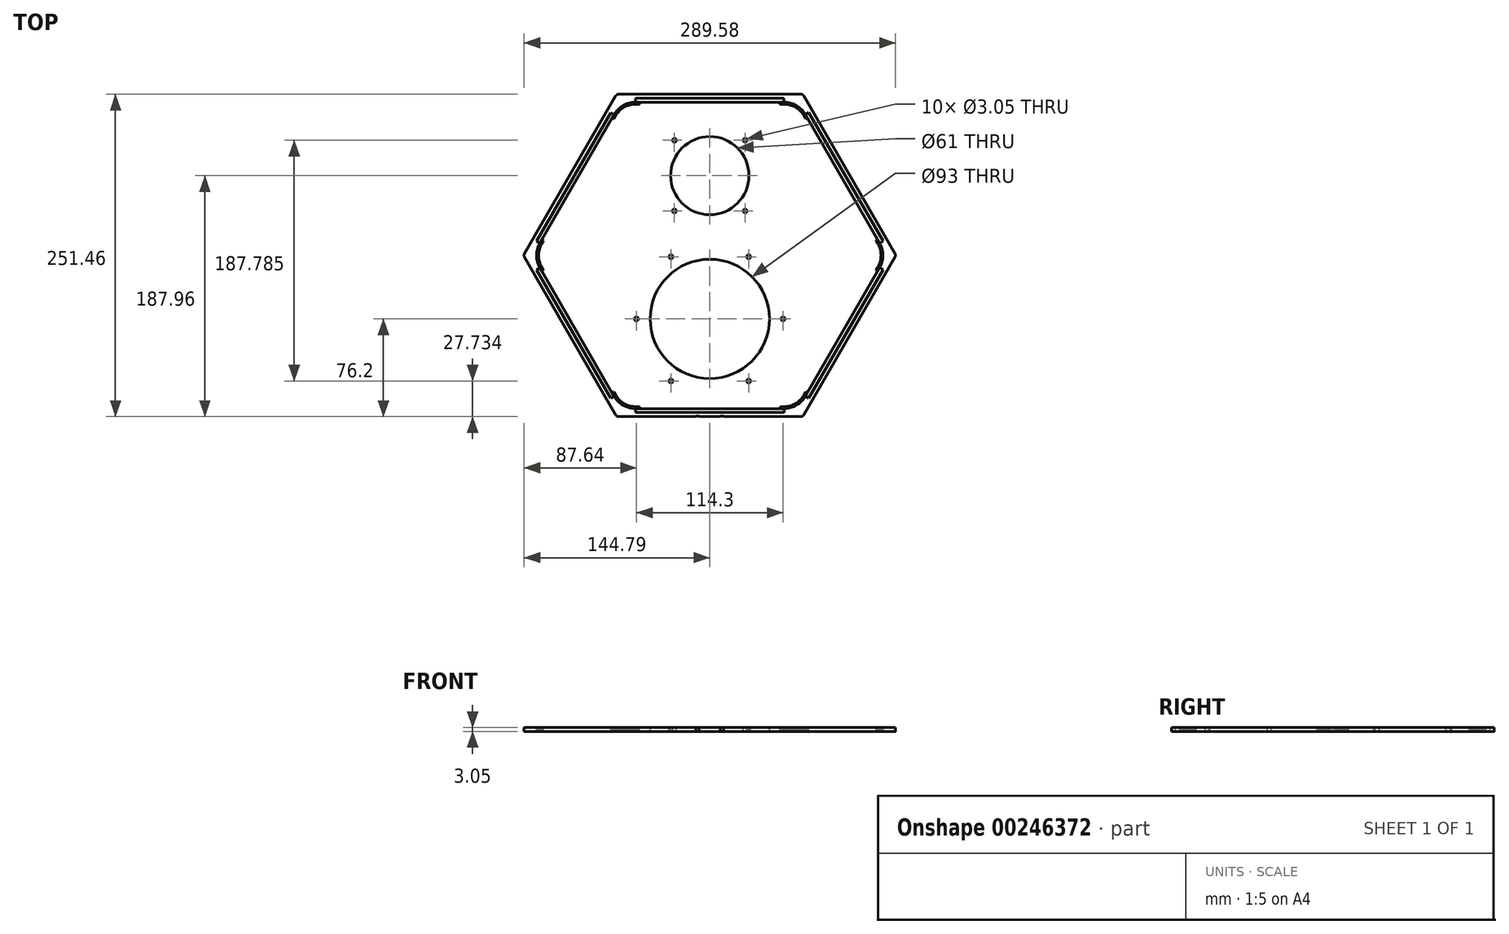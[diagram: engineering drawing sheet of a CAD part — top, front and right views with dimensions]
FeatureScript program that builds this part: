
annotation { "Feature Type Name" : "Feature", "Feature Type Description" : "" }
export const myFeature = defineFeature(function(context is Context, id is Id, definition is map)
    precondition{}
    {
        {
            var Q0;
            Q0=qCreatedBy(makeId("Top.planeOp"),FACE);
            var sketch = newSketch(context, id + "F0", { "sketchPlane" : qUnion([Q0])});
            skCircle(sketch, "E0.cCircle", {"center": v(0, 0) * mm, "radius": 125.73 * mm, "construction": true});
            skLineSegment(sketch, "E0.0", {"start": v(-137.85, 12.7) * mm, "end": v(-79.92, 113.03) * mm});
            skLineSegment(sketch, "E0.1", {"start": v(-57.93, 125.73) * mm, "end": v(57.93, 125.73) * mm});
            skLineSegment(sketch, "E0.2", {"start": v(79.92, 113.03) * mm, "end": v(137.85, 12.7) * mm});
            skLineSegment(sketch, "E0.3", {"start": v(137.85, -12.7) * mm, "end": v(79.92, -113.03) * mm});
            skLineSegment(sketch, "E0.4", {"start": v(57.93, -125.73) * mm, "end": v(-57.93, -125.73) * mm});
            skLineSegment(sketch, "E0.5", {"start": v(-79.92, -113.03) * mm, "end": v(-137.85, -12.7) * mm});
            skPoint(sketch, "E0.0.midPoint", {"position": v(-108.89, 62.87) * mm});
            skPoint(sketch, "E1.visualSharp", {"position": v(-72.6, 125.73) * mm});
            skArc(sketch, "E1.filletArc", {"start": v(-57.93, 125.73) * mm, "mid": v(-70.63, 122.33) * mm, "end": v(-79.92, 113.03) * mm});
            skPoint(sketch, "E2.visualSharp", {"position": v(72.6, 125.73) * mm});
            skArc(sketch, "E2.filletArc", {"start": v(79.92, 113.03) * mm, "mid": v(70.63, 122.33) * mm, "end": v(57.93, 125.73) * mm});
            skPoint(sketch, "E3.visualSharp", {"position": v(145.18, 0) * mm});
            skArc(sketch, "E3.filletArc", {"start": v(137.85, -12.7) * mm, "mid": v(141.25, 0) * mm, "end": v(137.85, 12.7) * mm});
            skPoint(sketch, "E4.visualSharp", {"position": v(72.6, -125.73) * mm});
            skArc(sketch, "E4.filletArc", {"start": v(57.93, -125.73) * mm, "mid": v(70.63, -122.33) * mm, "end": v(79.92, -113.03) * mm});
            skPoint(sketch, "E5.visualSharp", {"position": v(-72.6, -125.73) * mm});
            skArc(sketch, "E5.filletArc", {"start": v(-79.92, -113.03) * mm, "mid": v(-70.63, -122.33) * mm, "end": v(-57.93, -125.73) * mm});
            skPoint(sketch, "E6.visualSharp", {"position": v(-145.18, 0) * mm});
            skArc(sketch, "E6.filletArc", {"start": v(-137.85, 12.7) * mm, "mid": v(-141.25, 0) * mm, "end": v(-137.85, -12.7) * mm});
            skSolve(sketch);
        }
        {
            var Q0;
            Q0=qSketchRegion(id+"F0",true);
            extrude(context, id + "F1", {"entities" : qUnion([Q0]), "depth" : 3.05 * mm});
        }
        {
            var Q0;
            Q0=makeQuery(id+"F1.opExtrude","CAP_FACE",FACE,{"disambiguationData":[OSD([sQuery(id+"F0.wireOp",EDGE,"E0.0"),sQuery(id+"F0.wireOp",EDGE,"E0.1"),sQuery(id+"F0.wireOp",EDGE,"E0.2"),sQuery(id+"F0.wireOp",EDGE,"E0.3"),sQuery(id+"F0.wireOp",EDGE,"E0.4"),sQuery(id+"F0.wireOp",EDGE,"E0.5"),sQuery(id+"F0.wireOp",EDGE,"E1.filletArc"),sQuery(id+"F0.wireOp",EDGE,"E2.filletArc"),sQuery(id+"F0.wireOp",EDGE,"E3.filletArc"),sQuery(id+"F0.wireOp",EDGE,"E4.filletArc"),sQuery(id+"F0.wireOp",EDGE,"E5.filletArc"),sQuery(id+"F0.wireOp",EDGE,"E6.filletArc")])],"isStart":false});
            var sketch = newSketch(context, id + "F2", { "sketchPlane" : qUnion([Q0])});
            skCircle(sketch, "E7", {"center": v(0, 62.23) * mm, "radius": 30.5 * mm});
            skCircle(sketch, "E8", {"center": v(0, -49.53) * mm, "radius": 46.5 * mm});
            skLineSegment(sketch, "E9", {"start": v(-77.97, -49.53) * mm, "end": v(84.44, -49.53) * mm, "construction": true});
            skCircle(sketch, "E10", {"center": v(0, -49.53) * mm, "radius": 61.65 * mm, "construction": true});
            skCircle(sketch, "E11", {"center": v(0, -49.53) * mm, "radius": 57.15 * mm, "construction": true});
            skCircle(sketch, "E12", {"center": v(57.15, -49.53) * mm, "radius": 1.52 * mm});
            skLineSegment(sketch, "E13", {"start": v(0, -49.53) * mm, "end": v(0, -25.93) * mm, "construction": true});
            skLineSegment(sketch, "E14", {"start": v(0, -49.53) * mm, "end": v(30.28, -1.06) * mm, "construction": true});
            skLineSegment(sketch, "E15", {"start": v(0, -49.53) * mm, "end": v(30.28, -98) * mm, "construction": true});
            skCircle(sketch, "E16", {"center": v(30.28, -1.06) * mm, "radius": 1.52 * mm});
            skCircle(sketch, "E17", {"center": v(30.28, -98) * mm, "radius": 1.52 * mm});
            skCircle(sketch, "E18.MirrorC", {"center": v(-30.28, -1.06) * mm, "radius": 1.52 * mm});
            skCircle(sketch, "E19.MirrorC", {"center": v(-30.28, -98) * mm, "radius": 1.52 * mm});
            skCircle(sketch, "E20.MirrorC", {"center": v(-57.15, -49.53) * mm, "radius": 1.52 * mm});
            skCircle(sketch, "E21", {"center": v(0, 62.23) * mm, "radius": 38.97 * mm, "construction": true});
            skLineSegment(sketch, "E22", {"start": v(0, 62.23) * mm, "end": v(-27.56, 89.79) * mm, "construction": true});
            skCircle(sketch, "E23", {"center": v(-27.56, 89.79) * mm, "radius": 1.52 * mm});
            skCircle(sketch, "E24", {"center": v(-27.56, 34.67) * mm, "radius": 1.52 * mm});
            skCircle(sketch, "E25", {"center": v(27.56, 34.67) * mm, "radius": 1.52 * mm});
            skCircle(sketch, "E26", {"center": v(27.56, 89.79) * mm, "radius": 1.52 * mm});
            skLineSegment(sketch, "E27", {"start": v(-27.56, 89.79) * mm, "end": v(27.56, 89.79) * mm, "construction": true});
            skSolve(sketch);
        }
        {
            var Q0;
            Q0=qSketchRegion(id+"F2",true);
            extrude(context, id + "F3", {"entities" : qUnion([Q0]), "operationType" : NewBodyOperationType.REMOVE, "oppositeDirection" : true, "depth" : 25.4 * mm});
        }
        {
            var Q0;
            Q0=makeQuery(id+"F1.opExtrude","CAP_FACE",FACE,{"disambiguationData":[OSD([sQuery(id+"F0.wireOp",EDGE,"E0.0"),sQuery(id+"F0.wireOp",EDGE,"E0.1"),sQuery(id+"F0.wireOp",EDGE,"E0.2"),sQuery(id+"F0.wireOp",EDGE,"E0.3"),sQuery(id+"F0.wireOp",EDGE,"E0.4"),sQuery(id+"F0.wireOp",EDGE,"E0.5"),sQuery(id+"F0.wireOp",EDGE,"E1.filletArc"),sQuery(id+"F0.wireOp",EDGE,"E2.filletArc"),sQuery(id+"F0.wireOp",EDGE,"E3.filletArc"),sQuery(id+"F0.wireOp",EDGE,"E4.filletArc"),sQuery(id+"F0.wireOp",EDGE,"E5.filletArc"),sQuery(id+"F0.wireOp",EDGE,"E6.filletArc")])],"isStart":false});
            var sketch = newSketch(context, id + "F4", { "sketchPlane" : qUnion([Q0])});
            skLineSegment(sketch, "E28", {"start": v(-57.93, 122.56) * mm, "end": v(-57.93, 119.5) * mm});
            skLineSegment(sketch, "E29", {"start": v(-57.93, 119.5) * mm, "end": v(57.8, 119.5) * mm});
            skLineSegment(sketch, "E30", {"start": v(57.8, 119.5) * mm, "end": v(57.8, 122.56) * mm});
            skLineSegment(sketch, "E31.1.0", {"start": v(-135.1, 11.11) * mm, "end": v(-132.46, 9.59) * mm});
            skLineSegment(sketch, "E31.1.1", {"start": v(-132.46, 9.59) * mm, "end": v(-74.6, 109.82) * mm});
            skLineSegment(sketch, "E31.1.2", {"start": v(-74.6, 109.82) * mm, "end": v(-77.23, 111.34) * mm});
            skLineSegment(sketch, "E31.2.0", {"start": v(-77.17, -111.44) * mm, "end": v(-74.53, -109.92) * mm});
            skLineSegment(sketch, "E31.2.1", {"start": v(-74.53, -109.92) * mm, "end": v(-132.4, -9.7) * mm});
            skLineSegment(sketch, "E31.2.2", {"start": v(-132.4, -9.7) * mm, "end": v(-135.04, -11.22) * mm});
            skLineSegment(sketch, "E31.3.0", {"start": v(57.93, -122.55) * mm, "end": v(57.93, -119.5) * mm});
            skLineSegment(sketch, "E31.3.1", {"start": v(57.93, -119.5) * mm, "end": v(-57.8, -119.5) * mm});
            skLineSegment(sketch, "E31.3.2", {"start": v(-57.8, -119.5) * mm, "end": v(-57.8, -122.55) * mm});
            skLineSegment(sketch, "E31.4.0", {"start": v(135.1, -11.11) * mm, "end": v(132.46, -9.59) * mm});
            skLineSegment(sketch, "E31.4.1", {"start": v(132.46, -9.59) * mm, "end": v(74.6, -109.82) * mm});
            skLineSegment(sketch, "E31.4.2", {"start": v(74.6, -109.82) * mm, "end": v(77.23, -111.34) * mm});
            skLineSegment(sketch, "E31.5.0", {"start": v(77.17, 111.44) * mm, "end": v(74.53, 109.92) * mm});
            skLineSegment(sketch, "E31.5.1", {"start": v(74.53, 109.92) * mm, "end": v(132.4, 9.7) * mm});
            skLineSegment(sketch, "E31.5.2", {"start": v(132.4, 9.7) * mm, "end": v(135.04, 11.22) * mm});
            skPoint(sketch, "E31.center", {"position": v(0, 0) * mm});
            skLineSegment(sketch, "E32", {"start": v(-57.93, 122.56) * mm, "end": v(57.8, 122.56) * mm});
            skLineSegment(sketch, "E33.1.0", {"start": v(-135.1, 11.11) * mm, "end": v(-77.23, 111.34) * mm});
            skLineSegment(sketch, "E33.2.0", {"start": v(-77.17, -111.44) * mm, "end": v(-135.04, -11.22) * mm});
            skLineSegment(sketch, "E33.3.0", {"start": v(57.93, -122.56) * mm, "end": v(-57.8, -122.56) * mm});
            skLineSegment(sketch, "E33.4.0", {"start": v(135.1, -11.11) * mm, "end": v(77.23, -111.34) * mm});
            skLineSegment(sketch, "E33.5.0", {"start": v(77.17, 111.44) * mm, "end": v(135.04, 11.22) * mm});
            skSolve(sketch);
        }
        {
            var Q0;
            Q0=makeQuery(id+"F4.imprint","IMPRINT",FACE,{"disambiguationData":[TD([[makeQuery(id+"F4.imprint","IMPRINT",EDGE,{"derivedFrom":sQuery(id+"F4.wireOp",EDGE,"E31.2.0")}),1.0]])]});
            var Q1;
            Q1=makeQuery(id+"F4.imprint","IMPRINT",FACE,{"disambiguationData":[TD([[makeQuery(id+"F4.imprint","IMPRINT",EDGE,{"derivedFrom":sQuery(id+"F4.wireOp",EDGE,"E31.1.0")}),1.0]])]});
            var Q2;
            Q2=makeQuery(id+"F4.imprint","IMPRINT",FACE,{"disambiguationData":[TD([[makeQuery(id+"F4.imprint","IMPRINT",EDGE,{"derivedFrom":sQuery(id+"F4.wireOp",EDGE,"E28")}),1.0]])]});
            var Q3;
            Q3=makeQuery(id+"F4.imprint","IMPRINT",FACE,{"disambiguationData":[TD([[makeQuery(id+"F4.imprint","IMPRINT",EDGE,{"derivedFrom":sQuery(id+"F4.wireOp",EDGE,"E31.5.0")}),1.0]])]});
            var Q4;
            Q4=makeQuery(id+"F4.imprint","IMPRINT",FACE,{"disambiguationData":[TD([[makeQuery(id+"F4.imprint","IMPRINT",EDGE,{"derivedFrom":sQuery(id+"F4.wireOp",EDGE,"E31.4.0")}),1.0]])]});
            var Q5;
            Q5=makeQuery(id+"F4.imprint","IMPRINT",FACE,{"disambiguationData":[TD([[makeQuery(id+"F4.imprint","IMPRINT",EDGE,{"derivedFrom":sQuery(id+"F4.wireOp",EDGE,"E31.3.0")}),1.0]])]});
            extrude(context, id + "F5", {"entities" : qUnion([Q0, Q1, Q2, Q3, Q4, Q5]), "operationType" : NewBodyOperationType.REMOVE, "endBound" : BoundingType.THROUGH_ALL, "oppositeDirection" : true, "depth" : 25.4 * mm});
        }
        {
            var Q0;
            Q0=makeQuery(id+"F4.imprint","IMPRINT",FACE,{"disambiguationData":[TD([[makeQuery(id+"F4.imprint","IMPRINT",EDGE,{"derivedFrom":sQuery(id+"F4.wireOp",EDGE,"E28")}),-1.0]])]});
            var sketch = newSketch(context, id + "F6", { "sketchPlane" : qUnion([Q0])});
            skCircle(sketch, "E34", {"center": v(-62.3, 107.85) * mm, "radius": 7.89 * mm});
            skArc(sketch, "E35", {"start": v(-57.93, 119.5) * mm, "mid": v(-67.57, 116.9) * mm, "end": v(-74.6, 109.82) * mm, "construction": true});
            skLineSegment(sketch, "E36", {"start": v(-67.57, 116.9) * mm, "end": v(-62.3, 107.85) * mm, "construction": true});
            skPoint(sketch, "E37", {"position": v(-66.26, 114.67) * mm});
            skCircle(sketch, "E38.1.0", {"center": v(-124.55, -0.03) * mm, "radius": 7.89 * mm});
            skCircle(sketch, "E38.2.0", {"center": v(-62.25, -107.88) * mm, "radius": 7.89 * mm});
            skCircle(sketch, "E38.3.0", {"center": v(62.3, -107.85) * mm, "radius": 7.89 * mm});
            skCircle(sketch, "E38.4.0", {"center": v(124.55, 0.03) * mm, "radius": 7.89 * mm});
            skCircle(sketch, "E38.5.0", {"center": v(62.25, 107.88) * mm, "radius": 7.89 * mm});
            skPoint(sketch, "E38.center", {"position": v(0, 0) * mm});
            skSolve(sketch);
        }
        {
            var Q0;
            Q0=makeQuery(id+"F1.opExtrude","CAP_FACE",FACE,{"disambiguationData":[OSD([sQuery(id+"F0.wireOp",EDGE,"E0.0"),sQuery(id+"F0.wireOp",EDGE,"E0.1"),sQuery(id+"F0.wireOp",EDGE,"E0.2"),sQuery(id+"F0.wireOp",EDGE,"E0.3"),sQuery(id+"F0.wireOp",EDGE,"E0.4"),sQuery(id+"F0.wireOp",EDGE,"E0.5"),sQuery(id+"F0.wireOp",EDGE,"E1.filletArc"),sQuery(id+"F0.wireOp",EDGE,"E2.filletArc"),sQuery(id+"F0.wireOp",EDGE,"E3.filletArc"),sQuery(id+"F0.wireOp",EDGE,"E4.filletArc"),sQuery(id+"F0.wireOp",EDGE,"E5.filletArc"),sQuery(id+"F0.wireOp",EDGE,"E6.filletArc")])],"isStart":false});
            var sketch = newSketch(context, id + "F7", { "sketchPlane" : qUnion([Q0])});
            skPoint(sketch, "E39", {"position": v(0, -122.56) * mm});
            skPoint(sketch, "E40", {"position": v(9.58, -122.56) * mm});
            skPoint(sketch, "E41", {"position": v(-9.53, -122.56) * mm});
            skLineSegment(sketch, "E42.bottom", {"start": v(-10.8, -125.73) * mm, "end": v(-8.26, -125.73) * mm});
            skLineSegment(sketch, "E42.top", {"start": v(-10.8, -125.48) * mm, "end": v(-8.25, -125.48) * mm});
            skLineSegment(sketch, "E42.left", {"start": v(-10.8, -125.73) * mm, "end": v(-10.8, -125.48) * mm});
            skLineSegment(sketch, "E42.right", {"start": v(-8.25, -125.73) * mm, "end": v(-8.25, -125.48) * mm});
            skLineSegment(sketch, "E43.bottom", {"start": v(8.31, -125.73) * mm, "end": v(10.85, -125.73) * mm});
            skLineSegment(sketch, "E43.top", {"start": v(8.31, -125.48) * mm, "end": v(10.85, -125.48) * mm});
            skLineSegment(sketch, "E43.left", {"start": v(8.31, -125.73) * mm, "end": v(8.31, -125.48) * mm});
            skLineSegment(sketch, "E43.right", {"start": v(10.85, -125.73) * mm, "end": v(10.85, -125.48) * mm});
            skPoint(sketch, "E44", {"position": v(-9.53, -125.48) * mm});
            skPoint(sketch, "E45", {"position": v(9.58, -125.48) * mm});
            skSolve(sketch);
        }
        {
            var Q0;
            Q0=qSketchRegion(id+"F7",true);
            extrude(context, id + "F8", {"entities" : qUnion([Q0]), "operationType" : NewBodyOperationType.REMOVE, "endBound" : BoundingType.THROUGH_ALL, "oppositeDirection" : true, "depth" : 25.4 * mm});
        }
        {
            var Q0;
            Q0=makeQuery(id+"F1.opExtrude","CAP_FACE",FACE,{"disambiguationData":[OSD([sQuery(id+"F0.wireOp",EDGE,"E0.0"),sQuery(id+"F0.wireOp",EDGE,"E0.1"),sQuery(id+"F0.wireOp",EDGE,"E0.2"),sQuery(id+"F0.wireOp",EDGE,"E0.3"),sQuery(id+"F0.wireOp",EDGE,"E0.4"),sQuery(id+"F0.wireOp",EDGE,"E0.5"),sQuery(id+"F0.wireOp",EDGE,"E1.filletArc"),sQuery(id+"F0.wireOp",EDGE,"E2.filletArc"),sQuery(id+"F0.wireOp",EDGE,"E3.filletArc"),sQuery(id+"F0.wireOp",EDGE,"E4.filletArc"),sQuery(id+"F0.wireOp",EDGE,"E5.filletArc"),sQuery(id+"F0.wireOp",EDGE,"E6.filletArc")])],"isStart":false});
            var sketch = newSketch(context, id + "F9", { "sketchPlane" : qUnion([Q0])});
            skLineSegment(sketch, "E46", {"start": v(-79.92, 113.03) * mm, "end": v(-73.32, 124.46) * mm});
            skLineSegment(sketch, "E47", {"start": v(-71.12, 125.73) * mm, "end": v(-57.93, 125.73) * mm});
            skPoint(sketch, "E48.visualSharp", {"position": v(-72.6, 125.73) * mm});
            skArc(sketch, "E48.filletArc", {"start": v(-71.12, 125.73) * mm, "mid": v(-72.4, 125.39) * mm, "end": v(-73.32, 124.46) * mm});
            skLineSegment(sketch, "E49", {"start": v(-79.92, 113.03) * mm, "end": v(-57.93, 125.73) * mm});
            skLineSegment(sketch, "E50", {"start": v(57.93, 125.73) * mm, "end": v(71.12, 125.73) * mm});
            skLineSegment(sketch, "E51", {"start": v(73.32, 124.46) * mm, "end": v(79.92, 113.03) * mm});
            skLineSegment(sketch, "E52", {"start": v(-137.85, -12.7) * mm, "end": v(-144.45, -1.27) * mm});
            skLineSegment(sketch, "E53", {"start": v(-144.45, 1.27) * mm, "end": v(-137.85, 12.7) * mm});
            skLineSegment(sketch, "E54", {"start": v(57.93, -125.73) * mm, "end": v(71.12, -125.73) * mm});
            skLineSegment(sketch, "E55", {"start": v(73.32, -124.46) * mm, "end": v(79.92, -113.03) * mm});
            skLineSegment(sketch, "E56", {"start": v(137.85, 12.7) * mm, "end": v(144.45, 1.27) * mm});
            skLineSegment(sketch, "E57", {"start": v(144.45, -1.27) * mm, "end": v(137.85, -12.7) * mm});
            skPoint(sketch, "E58.visualSharp", {"position": v(72.6, 125.73) * mm});
            skArc(sketch, "E58.filletArc", {"start": v(73.32, 124.46) * mm, "mid": v(72.4, 125.39) * mm, "end": v(71.12, 125.73) * mm});
            skPoint(sketch, "E59.visualSharp", {"position": v(145.18, 0) * mm});
            skArc(sketch, "E59.filletArc", {"start": v(144.45, -1.27) * mm, "mid": v(144.79, 0) * mm, "end": v(144.45, 1.27) * mm});
            skPoint(sketch, "E60.visualSharp", {"position": v(72.6, -125.73) * mm});
            skArc(sketch, "E60.filletArc", {"start": v(71.12, -125.73) * mm, "mid": v(72.4, -125.39) * mm, "end": v(73.32, -124.46) * mm});
            skLineSegment(sketch, "E61", {"start": v(-79.92, -113.03) * mm, "end": v(-73.32, -124.46) * mm});
            skLineSegment(sketch, "E62", {"start": v(-71.12, -125.73) * mm, "end": v(-57.93, -125.73) * mm});
            skPoint(sketch, "E63.visualSharp", {"position": v(-72.6, -125.73) * mm});
            skArc(sketch, "E63.filletArc", {"start": v(-73.32, -124.46) * mm, "mid": v(-72.4, -125.39) * mm, "end": v(-71.12, -125.73) * mm});
            skPoint(sketch, "E64.visualSharp", {"position": v(-145.18, 0) * mm});
            skArc(sketch, "E64.filletArc", {"start": v(-144.45, 1.27) * mm, "mid": v(-144.79, 0) * mm, "end": v(-144.45, -1.27) * mm});
            skSolve(sketch);
        }
        {
            var Q0;
            Q0 = qSketchRegion(id + "F9", true);
            var Q1;
            Q1=makeQuery(id+"F9.imprint","IMPRINT",FACE,{"disambiguationData":[TD([[makeQuery(id+"F9.imprint","IMPRINT",EDGE,{"derivedFrom":sQuery(id+"F9.wireOp",EDGE,"E52")}),-1.0]])]});
            var Q2;
            Q2=makeQuery(id+"F9.imprint","IMPRINT",FACE,{"disambiguationData":[TD([[makeQuery(id+"F9.imprint","IMPRINT",EDGE,{"derivedFrom":sQuery(id+"F9.wireOp",EDGE,"E61")}),1.0]])]});
            var Q3;
            Q3=makeQuery(id+"F9.imprint","IMPRINT",FACE,{"disambiguationData":[TD([[makeQuery(id+"F9.imprint","IMPRINT",EDGE,{"derivedFrom":sQuery(id+"F9.wireOp",EDGE,"E54")}),1.0]])]});
            var Q4;
            Q4=makeQuery(id+"F9.imprint","IMPRINT",FACE,{"disambiguationData":[TD([[makeQuery(id+"F9.imprint","IMPRINT",EDGE,{"derivedFrom":sQuery(id+"F9.wireOp",EDGE,"E56")}),-1.0]])]});
            var Q5;
            Q5=makeQuery(id+"F9.imprint","IMPRINT",FACE,{"disambiguationData":[TD([[makeQuery(id+"F9.imprint","IMPRINT",EDGE,{"derivedFrom":sQuery(id+"F9.wireOp",EDGE,"E50")}),-1.0]])]});
            extrude(context, id + "F10", {"entities" : qUnion([Q0, Q1, Q2, Q3, Q4, Q5]), "operationType" : NewBodyOperationType.ADD, "oppositeDirection" : true, "depth" : 3.05 * mm});
        }
        {
            var Q0;
            {var subQ0=sQuery(id+"F0.wireOp",EDGE,"E5.filletArc");var subQ1=sQuery(id+"F0.wireOp",EDGE,"E3.filletArc");var subQ2=sQuery(id+"F0.wireOp",EDGE,"E4.filletArc");var subQ3=sQuery(id+"F0.wireOp",EDGE,"E6.filletArc");var subQ4=sQuery(id+"F0.wireOp",EDGE,"E2.filletArc");Q0=makeQuery(id+"F10.boolean.opBoolean","MERGE",FACE,{"derivedFrom":[makeQuery(id+"F1.opExtrude","CAP_FACE",FACE,{"disambiguationData":[OSD([sQuery(id+"F0.wireOp",EDGE,"E0.0"),sQuery(id+"F0.wireOp",EDGE,"E0.1"),sQuery(id+"F0.wireOp",EDGE,"E0.2"),sQuery(id+"F0.wireOp",EDGE,"E0.3"),sQuery(id+"F0.wireOp",EDGE,"E0.4"),sQuery(id+"F0.wireOp",EDGE,"E0.5"),sQuery(id+"F0.wireOp",EDGE,"E1.filletArc"),subQ4,subQ1,subQ2,subQ0,subQ3])],"isStart":false}),makeQuery(id+"F10.opExtrude","CAP_FACE",FACE,{"disambiguationData":[OSD([sQuery(id+"F9.wireOp",EDGE,"E46"),sQuery(id+"F9.wireOp",EDGE,"E47"),sQuery(id+"F9.wireOp",EDGE,"E48.filletArc"),sQuery(id+"F9.wireOp",EDGE,"E49")])],"isStart":true}),makeQuery(id+"F10.opExtrude","CAP_FACE",FACE,{"disambiguationData":[OSD([subQ4,sQuery(id+"F9.wireOp",EDGE,"E50"),sQuery(id+"F9.wireOp",EDGE,"E51"),sQuery(id+"F9.wireOp",EDGE,"E58.filletArc")])],"isStart":true}),makeQuery(id+"F10.opExtrude","CAP_FACE",FACE,{"disambiguationData":[OSD([subQ3,sQuery(id+"F9.wireOp",EDGE,"E52"),sQuery(id+"F9.wireOp",EDGE,"E53"),sQuery(id+"F9.wireOp",EDGE,"E64.filletArc")])],"isStart":true}),makeQuery(id+"F10.opExtrude","CAP_FACE",FACE,{"disambiguationData":[OSD([subQ2,sQuery(id+"F9.wireOp",EDGE,"E54"),sQuery(id+"F9.wireOp",EDGE,"E55"),sQuery(id+"F9.wireOp",EDGE,"E60.filletArc")])],"isStart":true}),makeQuery(id+"F10.opExtrude","CAP_FACE",FACE,{"disambiguationData":[OSD([subQ1,sQuery(id+"F9.wireOp",EDGE,"E56"),sQuery(id+"F9.wireOp",EDGE,"E57"),sQuery(id+"F9.wireOp",EDGE,"E59.filletArc")])],"isStart":true}),makeQuery(id+"F10.opExtrude","CAP_FACE",FACE,{"disambiguationData":[OSD([subQ0,sQuery(id+"F9.wireOp",EDGE,"E61"),sQuery(id+"F9.wireOp",EDGE,"E62"),sQuery(id+"F9.wireOp",EDGE,"E63.filletArc")])],"isStart":true})]});}
            var sketch = newSketch(context, id + "F11", { "sketchPlane" : qUnion([Q0])});
            skArc(sketch, "E65", {"start": v(-57.93, 119.5) * mm, "mid": v(-67.57, 116.9) * mm, "end": v(-74.6, 109.82) * mm});
            skArc(sketch, "E66.0", {"start": v(-57.93, 117.98) * mm, "mid": v(-66.8, 115.6) * mm, "end": v(-73.27, 109.06) * mm});
            skLineSegment(sketch, "E67", {"start": v(-57.93, 117.98) * mm, "end": v(-57.93, 119.5) * mm});
            skLineSegment(sketch, "E68", {"start": v(-73.27, 109.06) * mm, "end": v(-74.6, 109.82) * mm});
            skArc(sketch, "E69", {"start": v(74.53, 109.92) * mm, "mid": v(67.45, 116.94) * mm, "end": v(57.8, 119.5) * mm});
            skArc(sketch, "E70", {"start": v(-132.46, 9.59) * mm, "mid": v(-135.03, -0.06) * mm, "end": v(-132.4, -9.7) * mm});
            skArc(sketch, "E71", {"start": v(-74.53, -109.92) * mm, "mid": v(-67.46, -116.97) * mm, "end": v(-57.8, -119.5) * mm});
            skArc(sketch, "E72", {"start": v(57.93, -119.5) * mm, "mid": v(67.55, -116.88) * mm, "end": v(74.6, -109.82) * mm});
            skArc(sketch, "E73", {"start": v(132.46, -9.59) * mm, "mid": v(135, 0.06) * mm, "end": v(132.4, 9.7) * mm});
            skArc(sketch, "E74.0", {"start": v(73.22, 109.15) * mm, "mid": v(66.69, 115.62) * mm, "end": v(57.8, 117.98) * mm});
            skArc(sketch, "E75.0", {"start": v(131.13, -8.83) * mm, "mid": v(133.47, 0.05) * mm, "end": v(131.08, 8.93) * mm});
            skArc(sketch, "E76.0", {"start": v(57.92, -117.98) * mm, "mid": v(66.78, -115.56) * mm, "end": v(73.27, -109.05) * mm});
            skArc(sketch, "E77.0", {"start": v(-73.21, -109.16) * mm, "mid": v(-66.7, -115.65) * mm, "end": v(-57.82, -117.98) * mm});
            skArc(sketch, "E78.0", {"start": v(-131.14, 8.83) * mm, "mid": v(-133.5, -0.05) * mm, "end": v(-131.08, -8.92) * mm});
            skLineSegment(sketch, "E79", {"start": v(-132.46, 9.59) * mm, "end": v(-131.14, 8.83) * mm});
            skLineSegment(sketch, "E80", {"start": v(-131.08, -8.92) * mm, "end": v(-132.4, -9.7) * mm});
            skLineSegment(sketch, "E81", {"start": v(-73.21, -109.16) * mm, "end": v(-74.53, -109.92) * mm});
            skLineSegment(sketch, "E82", {"start": v(-57.82, -117.98) * mm, "end": v(-57.8, -119.5) * mm});
            skLineSegment(sketch, "E83", {"start": v(57.92, -117.98) * mm, "end": v(57.93, -119.5) * mm});
            skLineSegment(sketch, "E84", {"start": v(131.13, -8.83) * mm, "end": v(132.46, -9.59) * mm});
            skLineSegment(sketch, "E85", {"start": v(131.08, 8.93) * mm, "end": v(132.4, 9.7) * mm});
            skLineSegment(sketch, "E86", {"start": v(73.27, -109.05) * mm, "end": v(74.6, -109.82) * mm});
            skLineSegment(sketch, "E87", {"start": v(57.8, 117.98) * mm, "end": v(57.8, 119.5) * mm});
            skLineSegment(sketch, "E88", {"start": v(73.22, 109.15) * mm, "end": v(74.53, 109.92) * mm});
            skLineSegment(sketch, "E89", {"start": v(-74.6, 109.82) * mm, "end": v(-76.18, 107.07) * mm});
            skLineSegment(sketch, "E90", {"start": v(-76.18, 107.07) * mm, "end": v(-74.84, 106.3) * mm});
            skLineSegment(sketch, "E91", {"start": v(-74.84, 106.3) * mm, "end": v(-73.27, 109.06) * mm});
            skLineSegment(sketch, "E92", {"start": v(-57.93, 119.5) * mm, "end": v(-54.75, 119.5) * mm});
            skLineSegment(sketch, "E93", {"start": v(-54.75, 119.5) * mm, "end": v(-54.75, 117.98) * mm});
            skLineSegment(sketch, "E94", {"start": v(-54.75, 117.98) * mm, "end": v(-57.93, 117.98) * mm});
            skLineSegment(sketch, "E95", {"start": v(-132.46, 9.59) * mm, "end": v(-130.87, 12.34) * mm});
            skLineSegment(sketch, "E96", {"start": v(-130.87, 12.34) * mm, "end": v(-129.56, 11.6) * mm});
            skLineSegment(sketch, "E97", {"start": v(-129.56, 11.6) * mm, "end": v(-131.14, 8.83) * mm});
            skLineSegment(sketch, "E98", {"start": v(-132.4, -9.7) * mm, "end": v(-130.81, -12.44) * mm});
            skLineSegment(sketch, "E99", {"start": v(-130.81, -12.44) * mm, "end": v(-129.5, -11.68) * mm});
            skLineSegment(sketch, "E100", {"start": v(-129.5, -11.68) * mm, "end": v(-131.08, -8.92) * mm});
            skLineSegment(sketch, "E101", {"start": v(-74.53, -109.92) * mm, "end": v(-76.12, -107.17) * mm});
            skLineSegment(sketch, "E102", {"start": v(-76.12, -107.17) * mm, "end": v(-74.8, -106.4) * mm});
            skLineSegment(sketch, "E103", {"start": v(-74.8, -106.4) * mm, "end": v(-73.21, -109.16) * mm});
            skLineSegment(sketch, "E104", {"start": v(-57.8, -119.5) * mm, "end": v(-54.63, -119.5) * mm});
            skLineSegment(sketch, "E105", {"start": v(-54.63, -119.5) * mm, "end": v(-54.63, -117.98) * mm});
            skLineSegment(sketch, "E106", {"start": v(-54.63, -117.98) * mm, "end": v(-57.82, -117.98) * mm});
            skLineSegment(sketch, "E107", {"start": v(57.93, -119.5) * mm, "end": v(54.75, -119.5) * mm});
            skLineSegment(sketch, "E108", {"start": v(54.75, -119.5) * mm, "end": v(54.75, -117.98) * mm});
            skLineSegment(sketch, "E109", {"start": v(54.75, -117.98) * mm, "end": v(57.92, -117.98) * mm});
            skLineSegment(sketch, "E110", {"start": v(74.6, -109.82) * mm, "end": v(76.18, -107.07) * mm});
            skLineSegment(sketch, "E111", {"start": v(76.18, -107.07) * mm, "end": v(74.86, -106.3) * mm});
            skLineSegment(sketch, "E112", {"start": v(74.86, -106.3) * mm, "end": v(73.27, -109.05) * mm});
            skLineSegment(sketch, "E113", {"start": v(132.46, -9.59) * mm, "end": v(130.87, -12.34) * mm});
            skLineSegment(sketch, "E114", {"start": v(130.87, -12.34) * mm, "end": v(129.55, -11.58) * mm});
            skLineSegment(sketch, "E115", {"start": v(129.55, -11.58) * mm, "end": v(131.13, -8.83) * mm});
            skLineSegment(sketch, "E116", {"start": v(132.4, 9.7) * mm, "end": v(130.81, 12.44) * mm});
            skLineSegment(sketch, "E117", {"start": v(130.81, 12.44) * mm, "end": v(129.5, 11.68) * mm});
            skLineSegment(sketch, "E118", {"start": v(129.5, 11.68) * mm, "end": v(131.08, 8.93) * mm});
            skLineSegment(sketch, "E119", {"start": v(74.53, 109.92) * mm, "end": v(76.12, 107.17) * mm});
            skLineSegment(sketch, "E120", {"start": v(76.12, 107.17) * mm, "end": v(74.8, 106.4) * mm});
            skLineSegment(sketch, "E121", {"start": v(74.8, 106.4) * mm, "end": v(73.22, 109.15) * mm});
            skLineSegment(sketch, "E122", {"start": v(57.8, 119.5) * mm, "end": v(54.63, 119.5) * mm});
            skLineSegment(sketch, "E123", {"start": v(54.63, 119.5) * mm, "end": v(54.63, 117.98) * mm});
            skLineSegment(sketch, "E124", {"start": v(54.63, 117.98) * mm, "end": v(57.8, 117.98) * mm});
            skSolve(sketch);
        }
        {
            var Q0;
            Q0 = qSketchRegion(id + "F11", true);
            extrude(context, id + "F12", {"entities" : qUnion([Q0]), "operationType" : NewBodyOperationType.REMOVE, "oppositeDirection" : true, "depth" : 1.59 * mm});
        }
    });
